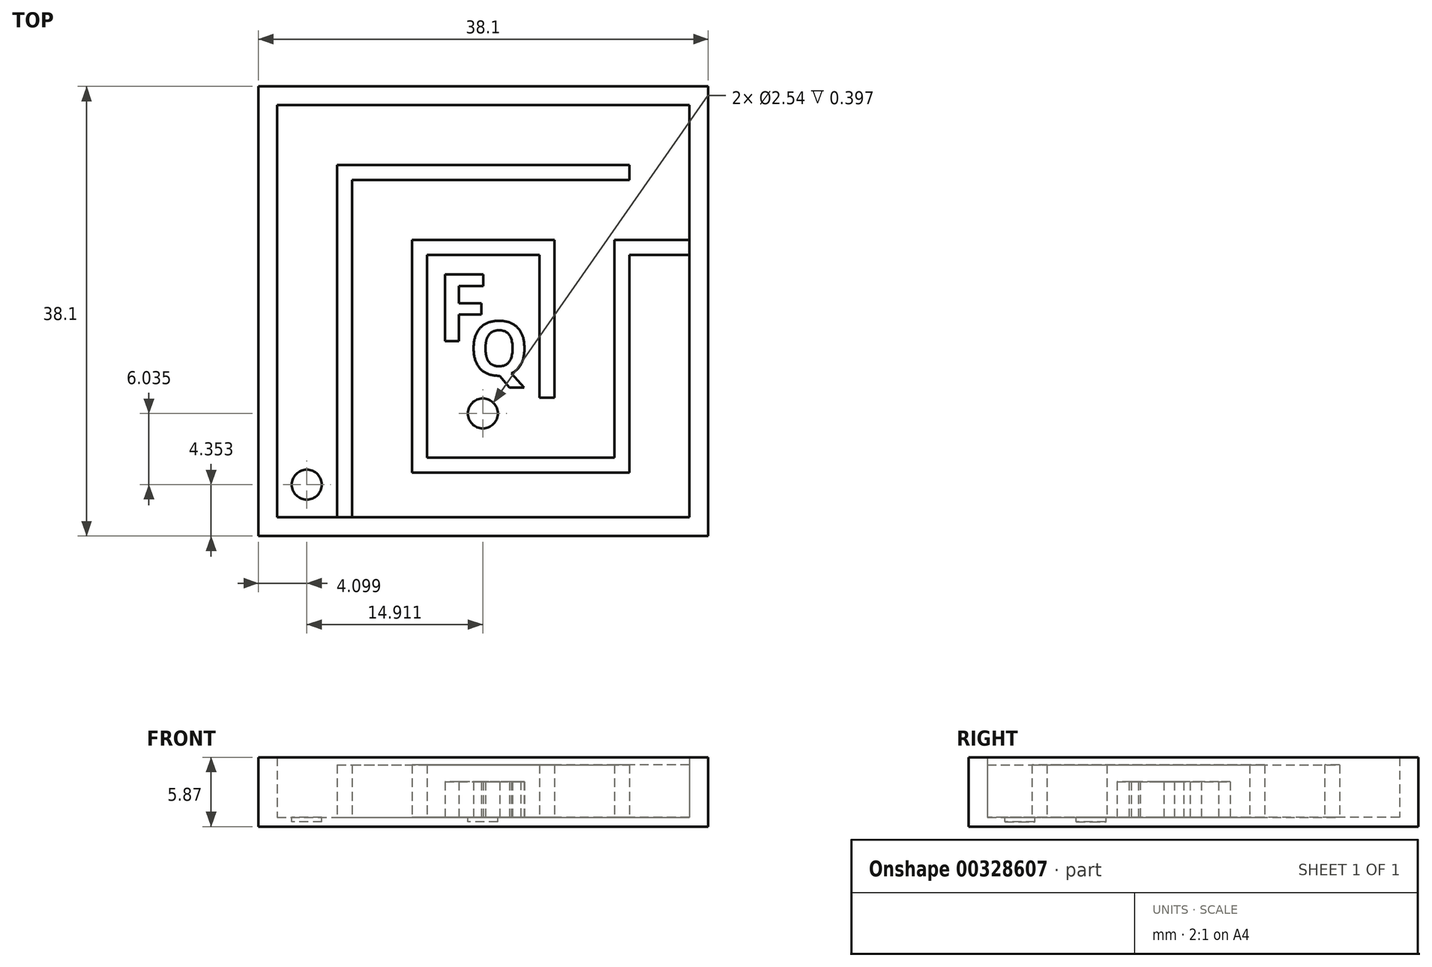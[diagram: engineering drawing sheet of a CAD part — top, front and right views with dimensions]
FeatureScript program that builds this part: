
annotation { "Feature Type Name" : "Feature", "Feature Type Description" : "" }
export const myFeature = defineFeature(function(context is Context, id is Id, definition is map)
    precondition{}
    {
        {
            var Q0;
            Q0=qCreatedBy(makeId("Top.planeOp"),FACE);
            var sketch = newSketch(context, id + "F0", { "sketchPlane" : qUnion([Q0])});
            skLineSegment(sketch, "E0.bottom", {"start": v(-7.03, 11.2) * mm, "end": v(31.07, 11.2) * mm});
            skLineSegment(sketch, "E0.top", {"start": v(-7.03, -26.9) * mm, "end": v(31.07, -26.9) * mm});
            skLineSegment(sketch, "E0.left", {"start": v(-7.03, 11.2) * mm, "end": v(-7.03, -26.9) * mm});
            skLineSegment(sketch, "E0.right", {"start": v(31.07, 11.2) * mm, "end": v(31.07, -26.9) * mm});
            skSolve(sketch);
        }
        {
            var Q0;
            Q0 = qSketchRegion(id + "F0", true);
            extrude(context, id + "F1", {"entities" : qUnion([Q0]), "depth" : 0.8 * mm});
        }
        {
            var Q0;
            Q0=makeQuery(id+"F1.opExtrude","CAP_FACE",FACE,{"disambiguationData":[OSD([sQuery(id+"F0.wireOp",EDGE,"E0.bottom"),sQuery(id+"F0.wireOp",EDGE,"E0.top"),sQuery(id+"F0.wireOp",EDGE,"E0.left"),sQuery(id+"F0.wireOp",EDGE,"E0.right")])],"isStart":false});
            var sketch = newSketch(context, id + "F2", { "sketchPlane" : qUnion([Q0])});
            skLineSegment(sketch, "E1.0", {"start": v(-5.45, 9.62) * mm, "end": v(29.48, 9.62) * mm});
            skLineSegment(sketch, "E1.1", {"start": v(-5.45, 9.62) * mm, "end": v(-5.45, -25.3) * mm});
            skLineSegment(sketch, "E1.2", {"start": v(-5.45, -25.3) * mm, "end": v(29.48, -25.3) * mm});
            skLineSegment(sketch, "E1.3", {"start": v(29.48, 9.62) * mm, "end": v(29.48, -25.3) * mm});
            skSolve(sketch);
        }
        {
            var Q0;
            Q0=makeQuery(id+"F2.imprint","IMPRINT",FACE,{"disambiguationData":[TD([[makeQuery(id+"F2.imprint","IMPRINT",EDGE,{"derivedFrom":sQuery(id+"F2.wireOp",EDGE,"E1.0")}),1.0]])]});
            extrude(context, id + "F3", {"entities" : qUnion([Q0]), "operationType" : NewBodyOperationType.ADD, "depth" : 5.08 * mm});
        }
        {
            var Q0;
            Q0=makeQuery(id+"F1.opExtrude","CAP_FACE",FACE,{"disambiguationData":[OSD([sQuery(id+"F0.wireOp",EDGE,"E0.bottom"),sQuery(id+"F0.wireOp",EDGE,"E0.top"),sQuery(id+"F0.wireOp",EDGE,"E0.left"),sQuery(id+"F0.wireOp",EDGE,"E0.right")])],"isStart":false});
            var sketch = newSketch(context, id + "F4", { "sketchPlane" : qUnion([Q0])});
            skLineSegment(sketch, "E2.top", {"start": v(-0.37, 4.54) * mm, "end": v(0.9, 4.54) * mm});
            skLineSegment(sketch, "E2.left", {"start": v(-0.37, -25.3) * mm, "end": v(-0.37, 4.54) * mm});
            skLineSegment(sketch, "E2.right", {"start": v(0.9, -25.3) * mm, "end": v(0.9, -14.01) * mm});
            skLineSegment(sketch, "E3.bottom", {"start": v(0.9, 4.54) * mm, "end": v(24.4, 4.54) * mm});
            skLineSegment(sketch, "E3.top", {"start": v(0.9, 3.27) * mm, "end": v(24.4, 3.27) * mm});
            skLineSegment(sketch, "E3.right", {"start": v(24.4, 4.54) * mm, "end": v(24.4, 3.27) * mm});
            skLineSegment(sketch, "E4.bottom", {"start": v(29.48, -1.8) * mm, "end": v(23.13, -1.8) * mm});
            skLineSegment(sketch, "E4.top", {"start": v(29.48, -3.08) * mm, "end": v(24.4, -3.08) * mm});
            skLineSegment(sketch, "E4.right", {"start": v(5.98, -1.8) * mm, "end": v(5.98, -3.08) * mm});
            skLineSegment(sketch, "E5.left", {"start": v(5.98, -3.08) * mm, "end": v(5.98, -12.74) * mm});
            skLineSegment(sketch, "E5.right", {"start": v(7.25, -3.08) * mm, "end": v(7.25, -14.01) * mm});
            skLineSegment(sketch, "E6.right", {"start": v(0.9, -14.01) * mm, "end": v(0.9, -12.74) * mm});
            skLineSegment(sketch, "E7.bottom", {"start": v(10.37, -3.08) * mm, "end": v(11.2, -3.08) * mm});
            skLineSegment(sketch, "E8.bottom", {"start": v(12.33, -1.8) * mm, "end": v(13.6, -1.8) * mm});
            skLineSegment(sketch, "E9.trimOffspring", {"start": v(0.9, -12.74) * mm, "end": v(0.9, 3.27) * mm});
            skLineSegment(sketch, "E10.top", {"start": v(18.05, -15.17) * mm, "end": v(16.78, -15.17) * mm});
            skLineSegment(sketch, "E10.left", {"start": v(18.05, -3.08) * mm, "end": v(18.05, -15.17) * mm});
            skLineSegment(sketch, "E10.right", {"start": v(16.78, -3.08) * mm, "end": v(16.78, -15.17) * mm});
            skLineSegment(sketch, "E11", {"start": v(5.98, -12.74) * mm, "end": v(5.98, -14.01) * mm});
            skLineSegment(sketch, "E12.top", {"start": v(7.25, -21.52) * mm, "end": v(5.98, -21.52) * mm});
            skLineSegment(sketch, "E12.left", {"start": v(7.25, -14.01) * mm, "end": v(7.25, -20.25) * mm});
            skLineSegment(sketch, "E12.right", {"start": v(5.98, -14.01) * mm, "end": v(5.98, -21.52) * mm});
            skLineSegment(sketch, "E13.bottom", {"start": v(7.25, -20.25) * mm, "end": v(23.13, -20.25) * mm});
            skLineSegment(sketch, "E13.top", {"start": v(7.25, -21.52) * mm, "end": v(23.13, -21.52) * mm});
            skLineSegment(sketch, "E14.bottom", {"start": v(23.13, -21.52) * mm, "end": v(24.4, -21.52) * mm});
            skLineSegment(sketch, "E14.left", {"start": v(23.13, -20.25) * mm, "end": v(23.13, -3.08) * mm});
            skLineSegment(sketch, "E14.right", {"start": v(24.4, -21.52) * mm, "end": v(24.4, -3.08) * mm});
            skLineSegment(sketch, "E15.trimOffspring", {"start": v(16.78, -3.08) * mm, "end": v(7.25, -3.08) * mm});
            skLineSegment(sketch, "E16", {"start": v(18.05, -3.08) * mm, "end": v(18.05, -1.8) * mm});
            skPoint(sketch, "E16.endSnap0", {"position": v(17.73, -1.8) * mm});
            skLineSegment(sketch, "E17", {"start": v(23.13, -3.08) * mm, "end": v(23.13, -1.8) * mm});
            skLineSegment(sketch, "E18.trimOffspring", {"start": v(18.05, -1.8) * mm, "end": v(5.98, -1.8) * mm});
            skSolve(sketch);
        }
        {
            var Q0;
            Q0=makeQuery(id+"F4.imprint","IMPRINT",FACE,{"disambiguationData":[TD([[makeQuery(id+"F4.imprint","IMPRINT",EDGE,{"derivedFrom":sQuery(id+"F4.wireOp",EDGE,"E2.top")}),1.0]])]});
            var sketch = newSketch(context, id + "F5", { "sketchPlane" : qUnion([Q0])});
            skCircle(sketch, "E19", {"center": v(-2.93, -22.54) * mm, "radius": 1.27 * mm});
            skPoint(sketch, "E19.centerSnap0", {"position": v(-2.93, -25.11) * mm});
            skCircle(sketch, "E20", {"center": v(11.98, -16.5) * mm, "radius": 1.27 * mm});
            skPoint(sketch, "E20.centerSnap0", {"position": v(11.98, -20.21) * mm});
            skSolve(sketch);
        }
        {
            var Q0;
            Q0 = qSketchRegion(id + "F4", true);
            var Q1;
            Q1=makeQuery(id+"F4.imprint","IMPRINT",FACE,{"disambiguationData":[TD([[makeQuery(id+"F4.imprint","IMPRINT",EDGE,{"derivedFrom":sQuery(id+"F4.wireOp",EDGE,"E2.top")}),-1.0]])]});
            extrude(context, id + "F6", {"entities" : qUnion([Q0, Q1]), "operationType" : NewBodyOperationType.ADD, "depth" : 4.44 * mm});
        }
        {
            var Q0;
            Q0 = qSketchRegion(id + "F4", true);
            var Q1;
            {var subQ8=sQuery(id+"F4.wireOp",EDGE,"E4.bottom");Q1=makeQuery(id+"F4.imprint","IMPRINT",FACE,{"disambiguationData":[TD([[makeQuery(id+"F4.imprint","IMPRINT",EDGE,{"derivedFrom":subQ8}),1.0]])]});}
            extrude(context, id + "F7", {"entities" : qUnion([Q0, Q1]), "operationType" : NewBodyOperationType.ADD, "depth" : 4.44 * mm});
        }
        {
            var Q0;
            Q0 = qSketchRegion(id + "F5", true);
            extrude(context, id + "F8", {"entities" : qUnion([Q0]), "operationType" : NewBodyOperationType.REMOVE, "oppositeDirection" : true, "depth" : 0.4 * mm});
        }
        {
            var Q0;
            Q0=qCreatedBy(makeId("Top.planeOp"),FACE);
            var sketch = newSketch(context, id + "F9", { "sketchPlane" : qUnion([Q0])});
            skText(sketch, "E21", { "text": "F", "fontName": "OpenSans-Bold.ttf"});
            skText(sketch, "E22", { "text": "Q", "fontName": "OpenSans-Bold.ttf"});
            const initialGuessF9  = {"E21": [0.00807, -0.01036, 1, 0, 0.00568], "E22": [0.01083, -0.01325, 1, 0, 0.00456]};
            skSetInitialGuess(sketch, initialGuessF9);
            skSolve(sketch);
        }
        {
            var Q0;
            Q0 = qSketchRegion(id + "F9", true);
            extrude(context, id + "F10", {"entities" : qUnion([Q0]), "operationType" : NewBodyOperationType.ADD, "depth" : 3.8 * mm});
        }
    });
